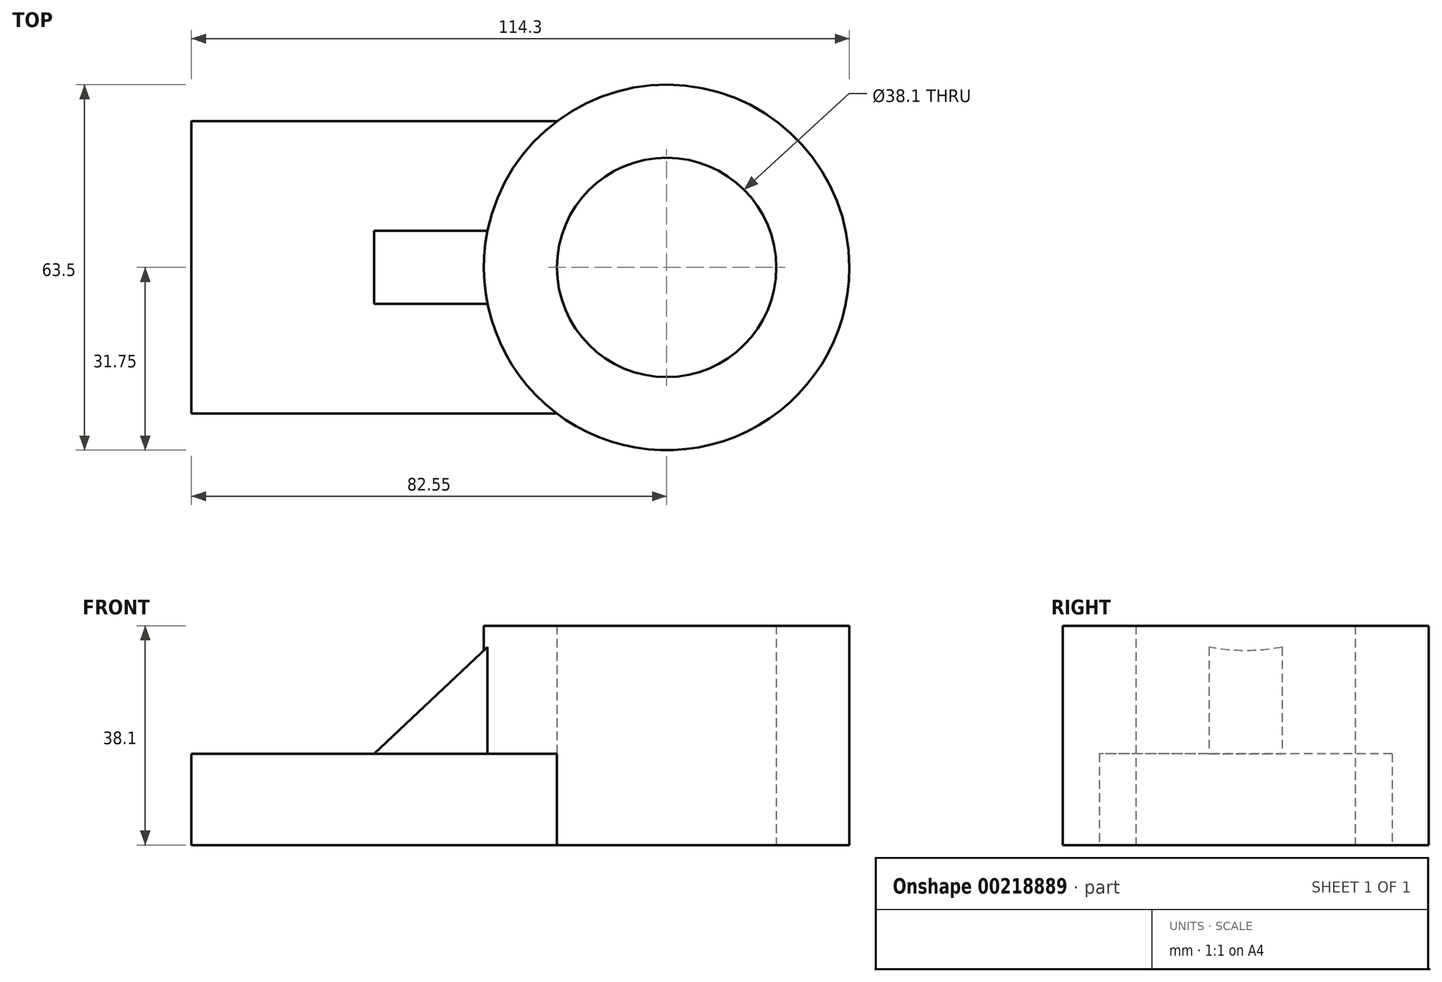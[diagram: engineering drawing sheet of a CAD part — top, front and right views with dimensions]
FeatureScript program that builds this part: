
annotation { "Feature Type Name" : "Feature", "Feature Type Description" : "" }
export const myFeature = defineFeature(function(context is Context, id is Id, definition is map)
    precondition{}
    {
        {
            var Q0;
            Q0=qCreatedBy(makeId("Top.planeOp"),FACE);
            var sketch = newSketch(context, id + "F0", { "sketchPlane" : qUnion([Q0])});
            skCircle(sketch, "E0", {"center": v(0, 0) * mm, "radius": 19.05 * mm});
            skCircle(sketch, "E1", {"center": v(0, 0) * mm, "radius": 31.75 * mm});
            skSolve(sketch);
        }
        {
            var Q0;
            Q0 = qSketchRegion(id + "F0", true);
            extrude(context, id + "F1", {"entities" : qUnion([Q0]), "depth" : 38.1 * mm});
        }
        {
            var Q0;
            Q0=makeQuery(id+"F1.opExtrude","CAP_FACE",FACE,{"disambiguationData":[OSD([sQuery(id+"F0.wireOp",EDGE,"E0"),sQuery(id+"F0.wireOp",EDGE,"E1")])],"isStart":true});
            var sketch = newSketch(context, id + "F2", { "sketchPlane" : qUnion([Q0])});
            skLineSegment(sketch, "E2", {"start": v(-19.05, -25.4) * mm, "end": v(-82.55, -25.4) * mm});
            skLineSegment(sketch, "E3", {"start": v(-82.55, -25.4) * mm, "end": v(-82.55, 25.4) * mm});
            skLineSegment(sketch, "E4", {"start": v(-82.55, 25.4) * mm, "end": v(-19.05, 25.4) * mm});
            skSolve(sketch);
        }
        {
            var Q0;
            {var subQ0=sQuery(id+"F2.wireOp",EDGE,"E2");Q0=makeQuery(id+"F2.imprint","IMPRINT",FACE,{"disambiguationData":[TD([[makeQuery(id+"F2.imprint","IMPRINT",EDGE,{"derivedFrom":subQ0}),-1.0]])]});}
            extrude(context, id + "F3", {"entities" : qUnion([Q0]), "operationType" : NewBodyOperationType.ADD, "oppositeDirection" : true, "depth" : 15.88 * mm});
        }
        {
            var Q0;
            Q0=qCreatedBy(makeId("Front.planeOp"),FACE);
            var sketch = newSketch(context, id + "F4", { "sketchPlane" : qUnion([Q0])});
            skLineSegment(sketch, "E5.0", {"start": v(-50.8, 15.88) * mm, "end": v(-30.75, 15.88) * mm});
            skLineSegment(sketch, "E6", {"start": v(-50.8, 15.88) * mm, "end": v(-30.75, 34.7) * mm});
            skLineSegment(sketch, "E7", {"start": v(-30.75, 34.7) * mm, "end": v(-30.75, 15.88) * mm});
            skPoint(sketch, "E8.orphan", {"position": v(-82.55, 15.88) * mm});
            skPoint(sketch, "E9.orphan", {"position": v(-19.05, 15.88) * mm});
            skSolve(sketch);
        }
        {
            var Q0;
            Q0 = qSketchRegion(id + "F4", true);
            extrude(context, id + "F5", {"entities" : qUnion([Q0]), "operationType" : NewBodyOperationType.ADD, "endBound" : BoundingType.SYMMETRIC, "depth" : 12.7 * mm});
        }
    });
